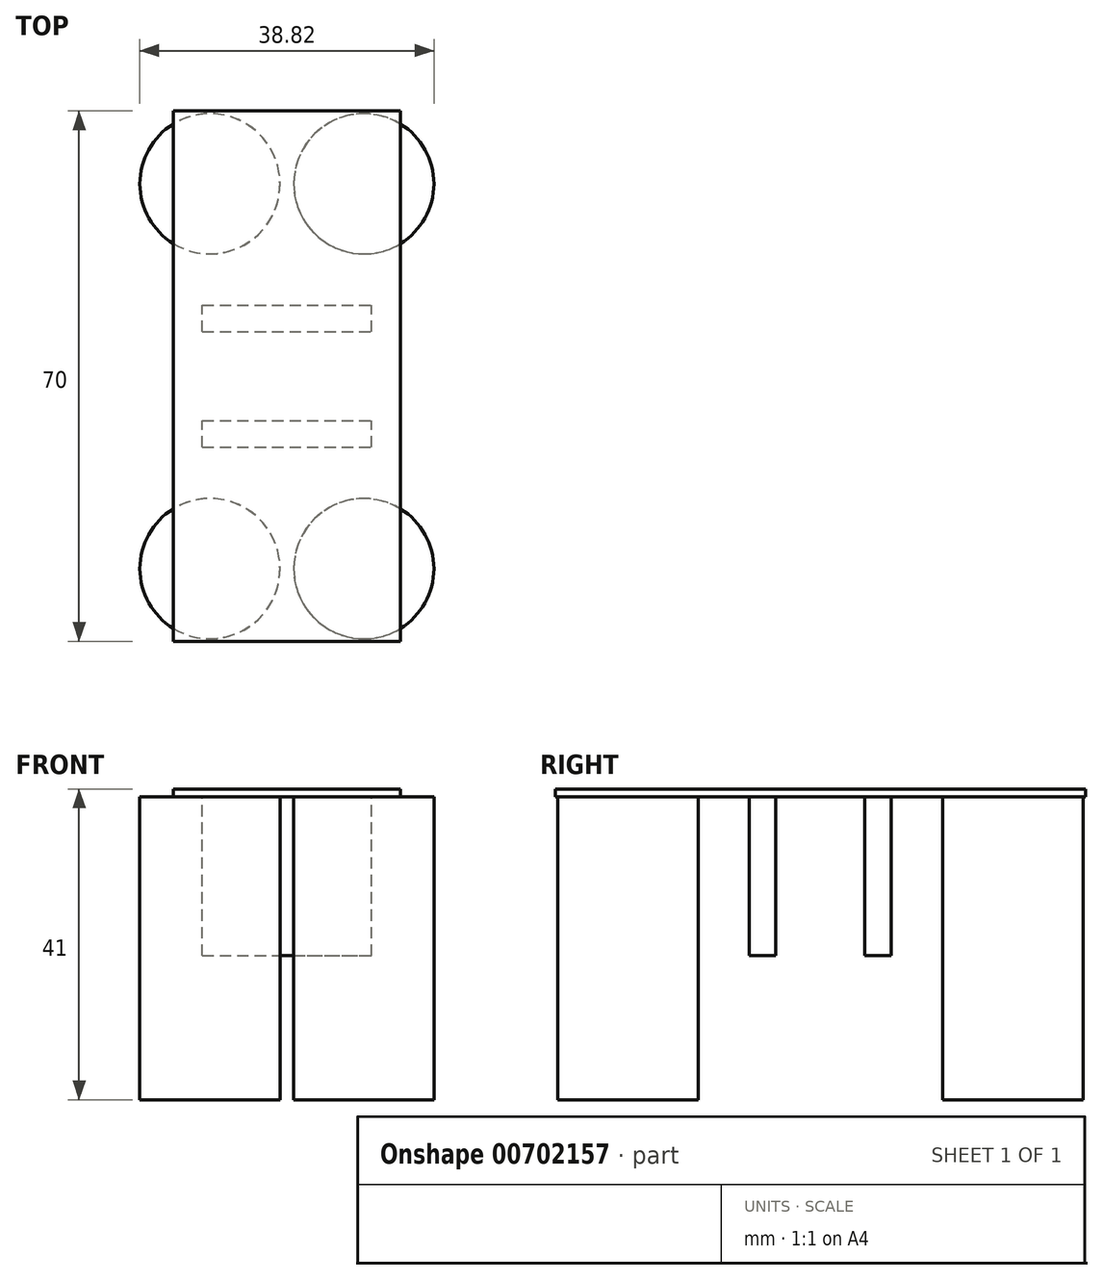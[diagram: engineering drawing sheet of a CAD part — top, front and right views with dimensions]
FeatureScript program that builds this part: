
annotation { "Feature Type Name" : "Feature", "Feature Type Description" : "" }
export const myFeature = defineFeature(function(context is Context, id is Id, definition is map)
    precondition{}
    {
        {
            var Q0;
            Q0=qCreatedBy(makeId("Top.planeOp"),FACE);
            var sketch = newSketch(context, id + "F0", { "sketchPlane" : qUnion([Q0])});
            skLineSegment(sketch, "E0.bottom", {"start": v(-15, 35) * mm, "end": v(15, 35) * mm});
            skLineSegment(sketch, "E0.top", {"start": v(-15, -35) * mm, "end": v(15, -35) * mm});
            skLineSegment(sketch, "E0.left", {"start": v(-15, 35) * mm, "end": v(-15, -35) * mm});
            skLineSegment(sketch, "E0.right", {"start": v(15, 35) * mm, "end": v(15, -35) * mm});
            skPoint(sketch, "E0.middle", {"position": v(0, 0) * mm});
            skSolve(sketch);
        }
        {
            var Q0;
            Q0 = qSketchRegion(id + "F0", true);
            extrude(context, id + "F1", {"entities" : qUnion([Q0]), "depth" : 1 * mm, "offsetDistance" : 25.4 * mm});
        }
        {
            var Q0;
            Q0=makeQuery(id+"F1.opExtrude","CAP_FACE",FACE,{"disambiguationData":[OSD([sQuery(id+"F0.wireOp",EDGE,"E0.bottom"),sQuery(id+"F0.wireOp",EDGE,"E0.top"),sQuery(id+"F0.wireOp",EDGE,"E0.left"),sQuery(id+"F0.wireOp",EDGE,"E0.right")])],"isStart":true});
            var sketch = newSketch(context, id + "F2", { "sketchPlane" : qUnion([Q0])});
            skSolve(sketch);
        }
        {
            var Q0;
            Q0=makeQuery(id+"F2.imprint","IMPRINT",FACE,{"disambiguationData":[TD([[makeQuery(id+"F2.imprint","IMPRINT",EDGE,{"derivedFrom":makeQuery(id+"F1.opExtrude","CAP_EDGE",EDGE,{"disambiguationData":[OSD([sQuery(id+"F0.wireOp",EDGE,"E0.bottom")])],"isStart":true})}),1.0]])]});
            var sketch = newSketch(context, id + "F3", { "sketchPlane" : qUnion([Q0])});
            skLineSegment(sketch, "E1.bottom", {"start": v(10.16, 25.4) * mm, "end": v(-10.16, 25.4) * mm, "construction": true});
            skLineSegment(sketch, "E1.top", {"start": v(10.16, -25.4) * mm, "end": v(-10.16, -25.4) * mm, "construction": true});
            skLineSegment(sketch, "E1.left", {"start": v(10.16, 25.4) * mm, "end": v(10.16, -25.4) * mm, "construction": true});
            skLineSegment(sketch, "E1.right", {"start": v(-10.16, 25.4) * mm, "end": v(-10.16, -25.4) * mm, "construction": true});
            skPoint(sketch, "E1.middle", {"position": v(0, 0) * mm});
            skCircle(sketch, "E2", {"center": v(10.16, 25.4) * mm, "radius": 9.25 * mm});
            skCircle(sketch, "E3", {"center": v(10.16, -25.4) * mm, "radius": 9.25 * mm});
            skCircle(sketch, "E4", {"center": v(-10.16, 25.4) * mm, "radius": 9.25 * mm});
            skCircle(sketch, "E5", {"center": v(-10.16, -25.4) * mm, "radius": 9.25 * mm});
            skLineSegment(sketch, "E6", {"start": v(-10.16, 29.15) * mm, "end": v(-10.16, 21.65) * mm, "construction": true});
            skLineSegment(sketch, "E7", {"start": v(10.16, 29.15) * mm, "end": v(10.16, 21.65) * mm, "construction": true});
            skLineSegment(sketch, "E8", {"start": v(-10.16, -21.65) * mm, "end": v(-10.16, -29.15) * mm, "construction": true});
            skLineSegment(sketch, "E9", {"start": v(10.16, -21.65) * mm, "end": v(10.16, -29.15) * mm, "construction": true});
            skLineSegment(sketch, "E10.bottom", {"start": v(-11.15, 9.37) * mm, "end": v(11.15, 9.37) * mm});
            skLineSegment(sketch, "E10.top", {"start": v(-11.15, 5.87) * mm, "end": v(11.15, 5.87) * mm});
            skLineSegment(sketch, "E10.left", {"start": v(-11.15, 9.37) * mm, "end": v(-11.15, 5.87) * mm});
            skLineSegment(sketch, "E10.right", {"start": v(11.15, 9.37) * mm, "end": v(11.15, 5.87) * mm});
            skPoint(sketch, "E10.middle", {"position": v(0, 7.62) * mm});
            skLineSegment(sketch, "E11.bottom", {"start": v(-11.15, -5.87) * mm, "end": v(11.15, -5.87) * mm});
            skLineSegment(sketch, "E11.top", {"start": v(-11.15, -9.37) * mm, "end": v(11.15, -9.37) * mm});
            skLineSegment(sketch, "E11.left", {"start": v(-11.15, -5.87) * mm, "end": v(-11.15, -9.37) * mm});
            skLineSegment(sketch, "E11.right", {"start": v(11.15, -5.87) * mm, "end": v(11.15, -9.37) * mm});
            skPoint(sketch, "E11.middle", {"position": v(0, -7.62) * mm});
            skLineSegment(sketch, "E12", {"start": v(0, 7.62) * mm, "end": v(0, -7.62) * mm, "construction": true});
            skSolve(sketch);
        }
        {
            var Q0;
            Q0=makeQuery(id+"F3.imprint","IMPRINT",FACE,{"disambiguationData":[TD([[makeQuery(id+"F3.imprint","IMPRINT",EDGE,{"derivedFrom":sQuery(id+"F3.wireOp",EDGE,"E10.bottom")}),-1.0]])]});
            var Q1;
            Q1=makeQuery(id+"F3.imprint","IMPRINT",FACE,{"disambiguationData":[TD([[makeQuery(id+"F3.imprint","IMPRINT",EDGE,{"derivedFrom":sQuery(id+"F3.wireOp",EDGE,"E11.bottom")}),-1.0]])]});
            extrude(context, id + "F4", {"entities" : qUnion([Q0, Q1]), "operationType" : NewBodyOperationType.ADD, "depth" : 21 * mm, "offsetDistance" : 25.4 * mm});
        }
        {
            var Q0;
            {var subQ0=sQuery(id+"F3.wireOp",EDGE,"E4");var subQ1=makeQuery(id+"F2.imprint","IMPRINT",EDGE,{"derivedFrom":makeQuery(id+"F1.opExtrude","CAP_EDGE",EDGE,{"disambiguationData":[OSD([sQuery(id+"F0.wireOp",EDGE,"E0.left")])],"isStart":true})});var subQ2=makeQuery(id+"F3.imprint","INTERSECT",VERTEX,{"disambiguationData":[OD(0.0)],"derivedFrom":[subQ1,subQ0]});Q0=makeQuery(id+"F3.imprint","IMPRINT",FACE,{"disambiguationData":[TD([[makeQuery(id+"F3.imprint","IMPRINT",EDGE,{"disambiguationData":[TD([[subQ2,1.0]])],"derivedFrom":subQ0}),1.0]])]});}
            var Q1;
            {var subQ0=sQuery(id+"F3.wireOp",EDGE,"E2");var subQ1=makeQuery(id+"F2.imprint","IMPRINT",EDGE,{"derivedFrom":makeQuery(id+"F1.opExtrude","CAP_EDGE",EDGE,{"disambiguationData":[OSD([sQuery(id+"F0.wireOp",EDGE,"E0.right")])],"isStart":true})});var subQ2=makeQuery(id+"F3.imprint","INTERSECT",VERTEX,{"disambiguationData":[OD(0.0)],"derivedFrom":[subQ1,subQ0]});Q1=makeQuery(id+"F3.imprint","IMPRINT",FACE,{"disambiguationData":[TD([[makeQuery(id+"F3.imprint","IMPRINT",EDGE,{"disambiguationData":[TD([[subQ2,-1.0]])],"derivedFrom":subQ0}),1.0]])]});}
            var Q2;
            {var subQ0=sQuery(id+"F3.wireOp",EDGE,"E5");var subQ1=makeQuery(id+"F2.imprint","IMPRINT",EDGE,{"derivedFrom":makeQuery(id+"F1.opExtrude","CAP_EDGE",EDGE,{"disambiguationData":[OSD([sQuery(id+"F0.wireOp",EDGE,"E0.left")])],"isStart":true})});var subQ2=makeQuery(id+"F3.imprint","INTERSECT",VERTEX,{"disambiguationData":[OD(0.0)],"derivedFrom":[subQ1,subQ0]});Q2=makeQuery(id+"F3.imprint","IMPRINT",FACE,{"disambiguationData":[TD([[makeQuery(id+"F3.imprint","IMPRINT",EDGE,{"disambiguationData":[TD([[subQ2,-1.0]])],"derivedFrom":subQ0}),1.0]])]});}
            var Q3;
            {var subQ0=sQuery(id+"F3.wireOp",EDGE,"E3");var subQ1=makeQuery(id+"F2.imprint","IMPRINT",EDGE,{"derivedFrom":makeQuery(id+"F1.opExtrude","CAP_EDGE",EDGE,{"disambiguationData":[OSD([sQuery(id+"F0.wireOp",EDGE,"E0.right")])],"isStart":true})});var subQ2=makeQuery(id+"F3.imprint","INTERSECT",VERTEX,{"disambiguationData":[OD(0.0)],"derivedFrom":[subQ1,subQ0]});Q3=makeQuery(id+"F3.imprint","IMPRINT",FACE,{"disambiguationData":[TD([[makeQuery(id+"F3.imprint","IMPRINT",EDGE,{"disambiguationData":[TD([[subQ2,1.0]])],"derivedFrom":subQ0}),1.0]])]});}
            var Q4;
            {var subQ0=sQuery(id+"F3.wireOp",EDGE,"E5");var subQ1=makeQuery(id+"F2.imprint","IMPRINT",EDGE,{"derivedFrom":makeQuery(id+"F1.opExtrude","CAP_EDGE",EDGE,{"disambiguationData":[OSD([sQuery(id+"F0.wireOp",EDGE,"E0.left")])],"isStart":true})});var subQ2=makeQuery(id+"F3.imprint","INTERSECT",VERTEX,{"disambiguationData":[OD(0.0)],"derivedFrom":[subQ1,subQ0]});Q4=makeQuery(id+"F3.imprint","IMPRINT",FACE,{"disambiguationData":[TD([[makeQuery(id+"F3.imprint","IMPRINT",EDGE,{"disambiguationData":[TD([[subQ2,1.0]])],"derivedFrom":subQ0}),1.0]])]});}
            var Q5;
            {var subQ0=sQuery(id+"F3.wireOp",EDGE,"E4");var subQ1=makeQuery(id+"F2.imprint","IMPRINT",EDGE,{"derivedFrom":makeQuery(id+"F1.opExtrude","CAP_EDGE",EDGE,{"disambiguationData":[OSD([sQuery(id+"F0.wireOp",EDGE,"E0.left")])],"isStart":true})});var subQ2=makeQuery(id+"F3.imprint","INTERSECT",VERTEX,{"disambiguationData":[OD(0.0)],"derivedFrom":[subQ1,subQ0]});Q5=makeQuery(id+"F3.imprint","IMPRINT",FACE,{"disambiguationData":[TD([[makeQuery(id+"F3.imprint","IMPRINT",EDGE,{"disambiguationData":[TD([[subQ2,-1.0]])],"derivedFrom":subQ0}),1.0]])]});}
            var Q6;
            {var subQ0=sQuery(id+"F3.wireOp",EDGE,"E2");var subQ1=makeQuery(id+"F2.imprint","IMPRINT",EDGE,{"derivedFrom":makeQuery(id+"F1.opExtrude","CAP_EDGE",EDGE,{"disambiguationData":[OSD([sQuery(id+"F0.wireOp",EDGE,"E0.right")])],"isStart":true})});var subQ2=makeQuery(id+"F3.imprint","INTERSECT",VERTEX,{"disambiguationData":[OD(0.0)],"derivedFrom":[subQ1,subQ0]});Q6=makeQuery(id+"F3.imprint","IMPRINT",FACE,{"disambiguationData":[TD([[makeQuery(id+"F3.imprint","IMPRINT",EDGE,{"disambiguationData":[TD([[subQ2,1.0]])],"derivedFrom":subQ0}),1.0]])]});}
            var Q7;
            {var subQ0=sQuery(id+"F3.wireOp",EDGE,"E3");var subQ1=makeQuery(id+"F2.imprint","IMPRINT",EDGE,{"derivedFrom":makeQuery(id+"F1.opExtrude","CAP_EDGE",EDGE,{"disambiguationData":[OSD([sQuery(id+"F0.wireOp",EDGE,"E0.right")])],"isStart":true})});var subQ2=makeQuery(id+"F3.imprint","INTERSECT",VERTEX,{"disambiguationData":[OD(0.0)],"derivedFrom":[subQ1,subQ0]});Q7=makeQuery(id+"F3.imprint","IMPRINT",FACE,{"disambiguationData":[TD([[makeQuery(id+"F3.imprint","IMPRINT",EDGE,{"disambiguationData":[TD([[subQ2,-1.0]])],"derivedFrom":subQ0}),1.0]])]});}
            extrude(context, id + "F5", {"entities" : qUnion([Q0, Q1, Q2, Q3, Q4, Q5, Q6, Q7]), "operationType" : NewBodyOperationType.ADD, "depth" : 40 * mm, "offsetDistance" : 25.4 * mm});
        }
    });
